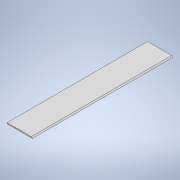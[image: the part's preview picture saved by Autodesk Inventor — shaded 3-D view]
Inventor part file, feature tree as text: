
AUTODESK INVENTOR PART (.ipt)
format: ipt  version: 2020 (Build 240168000, 168)  size: 95,744 bytes
history: native  units: in
note: dims shown in document units (in); Inventor stores cm internally (conversion verified against a paired STEP export)
features: extrude x1, chamfer x1, sketch x1
ambient origin geometry x8: Origin, YZ Plane, XZ Plane, XY Plane, X Axis, Y Axis, Z Axis, Center Point
bodies: Solid1 (feature_tree)
feature tree (3):
  extrude  "Extrusion1"  Depth=0.315in
  chamfer  "Chamfer1"  Distance=39.3701in
  sketch  "Sketch1"  dims[d0=7.0866in d1=3.5433in d2=39.3701in d3=19.685in d4=0.315in d5=0.0in d6=0.315in d7=0.0492in d8=45.0deg]
